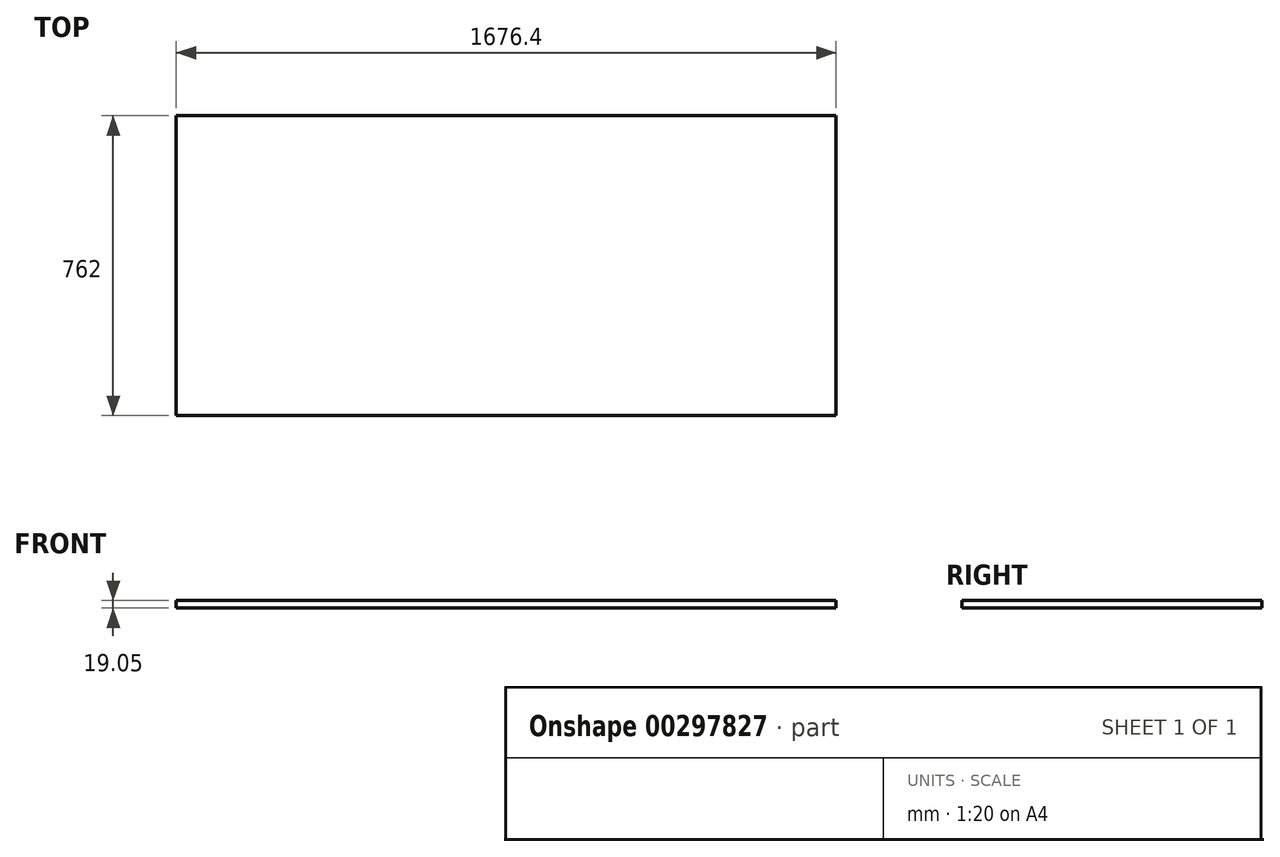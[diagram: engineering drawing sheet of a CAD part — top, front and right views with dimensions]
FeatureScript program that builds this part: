
annotation { "Feature Type Name" : "Feature", "Feature Type Description" : "" }
export const myFeature = defineFeature(function(context is Context, id is Id, definition is map)
    precondition{}
    {
        {
            var Q0;
            Q0=qCreatedBy(makeId("Top.planeOp"),FACE);
            var sketch = newSketch(context, id + "F0", { "sketchPlane" : qUnion([Q0])});
            skLineSegment(sketch, "E0.bottom", {"start": v(0, 0) * mm, "end": v(1676.4, 0) * mm});
            skLineSegment(sketch, "E0.top", {"start": v(0, 762) * mm, "end": v(1676.4, 762) * mm});
            skLineSegment(sketch, "E0.left", {"start": v(0, 0) * mm, "end": v(0, 762) * mm});
            skLineSegment(sketch, "E0.right", {"start": v(1676.4, 0) * mm, "end": v(1676.4, 762) * mm});
            skSolve(sketch);
        }
        {
            var Q0;
            Q0=makeQuery(id+"F0.imprint","IMPRINT",FACE,{"disambiguationData":[TD([[makeQuery(id+"F0.imprint","IMPRINT",EDGE,{"derivedFrom":sQuery(id+"F0.wireOp",EDGE,"E0.bottom")}),1.0]])]});
            extrude(context, id + "F1", {"entities" : qUnion([Q0]), "depth" : 19.05 * mm});
        }
    });
